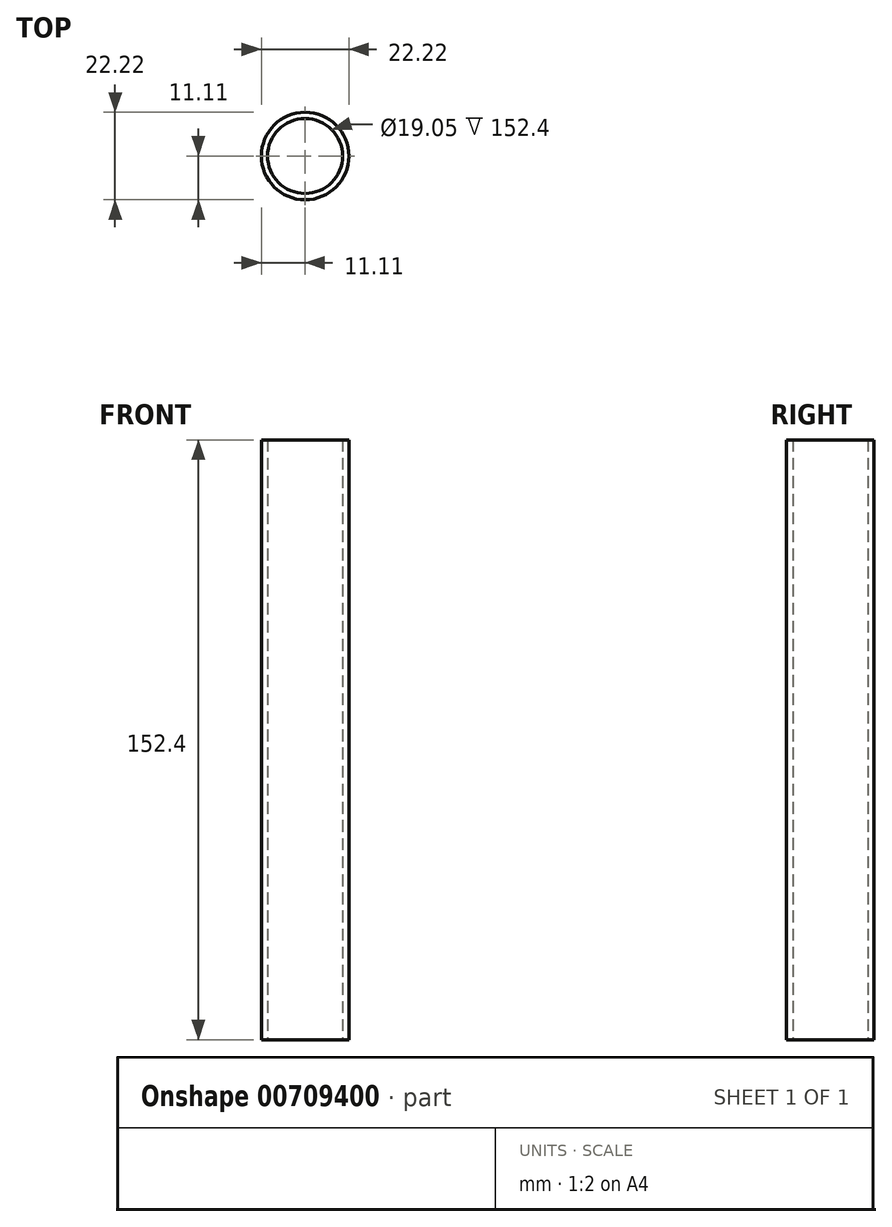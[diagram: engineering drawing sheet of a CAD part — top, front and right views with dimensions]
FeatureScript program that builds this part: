
annotation { "Feature Type Name" : "Feature", "Feature Type Description" : "" }
export const myFeature = defineFeature(function(context is Context, id is Id, definition is map)
    precondition{}
    {
        {
            var Q0;
            Q0=qCreatedBy(makeId("Top.planeOp"),FACE);
            var sketch = newSketch(context, id + "F0", { "sketchPlane" : qUnion([Q0])});
            skLineSegment(sketch, "E0", {"start": v(0, 0) * mm, "end": v(9.53, 0) * mm});
            skCircle(sketch, "E1", {"center": v(0, 0) * mm, "radius": 9.53 * mm});
            skCircle(sketch, "E2.0", {"center": v(0, 0) * mm, "radius": 11.11 * mm});
            skSolve(sketch);
        }
        {
            var Q0;
            Q0=qCreatedBy(makeId("Top.planeOp"),FACE);
            var sketch = newSketch(context, id + "F1", { "sketchPlane" : qUnion([Q0])});
            skSolve(sketch);
        }
        {
            var Q0;
            Q0=qSketchRegion(id+"F1",true);
            var Q1;
            Q1=makeQuery(id+"F0.imprint","IMPRINT",FACE,{"disambiguationData":[TD([[makeQuery(id+"F0.imprint","IMPRINT",EDGE,{"derivedFrom":sQuery(id+"F0.wireOp",EDGE,"E1")}),-1.0]])]});
            extrude(context, id + "F2", {"entities" : qUnion([Q0, Q1]), "depth" : 152.4 * mm, "offsetDistance" : 25.4 * mm});
        }
    });
